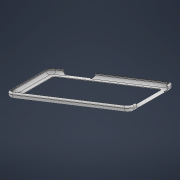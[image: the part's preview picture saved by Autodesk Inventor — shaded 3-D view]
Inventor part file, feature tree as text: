
AUTODESK INVENTOR PART (.ipt)
format: ipt  version: 2021 (Build 250183000, 183)  size: 458,752 bytes
history: native  units: mm
features: extrude x4, sketch x4, fillet x3, plane x2, thicken_offset x1, chamfer x1
ambient origin geometry x8: Origin, YZ Plane, XZ Plane, XY Plane, X Axis, Y Axis, Z Axis, Center Point
bodies: Solid1 (feature_tree), Solid2 (feature_tree)
feature tree (15):
  extrude  "Extrusion1"  Depth=137.5mm
  fillet  "Fillet1"  [1 undecoded]
  fillet  "Fillet2"  Radius=9.9mm
  fillet  "Fillet3"  Radius=0.98mm
  thicken_offset  "Thicken1"
  chamfer  "Chamfer2"  [1 undecoded]
  extrude  "Extrusion2"  Depth=10.0mm TaperAngle=0.0deg
  plane  "Work Plane1"
  extrude  "Extrusion3"  Depth=10.0mm TaperAngle=0.0deg
  plane  "Work Plane2"
  extrude  "Extrusion5"  Depth=2.0mm
  sketch  "Sketch1"  dims[d0=208.4mm d1=137.5mm d3=0.0mm d4=9.9mm d7=0.98mm d8=0.8mm d18=0.0mm d19=0.0mm]
  sketch  "Sketch3"  dims[d20=53.5mm d22=10.0mm d23=0.0mm]
  sketch  "Sketch4"  dims[d28=5.9mm d29=10.0mm d30=0.0mm]
  sketch  "Sketch5"  dims[d31=5.9mm d32=2.0mm d33=2.0mm d34=3.5mm d35=10.0mm d36=3.5mm d37=10.0mm d38=5.0mm d39=0.0mm d40=5.0mm d41=10.0mm d42=8.0mm d43=8.0mm d44=8.0mm d45=8.0mm d46=5.9mm d47=24.5mm d48=19.0mm d49=19.0mm d53=0.5mm d54=2.0mm d55=45.0deg]
note: 2 required parameter values undecoded (feature->parameter linkage not recoverable at this tier; creation-order binding heuristic only, values carry confidence <= 0.55)
